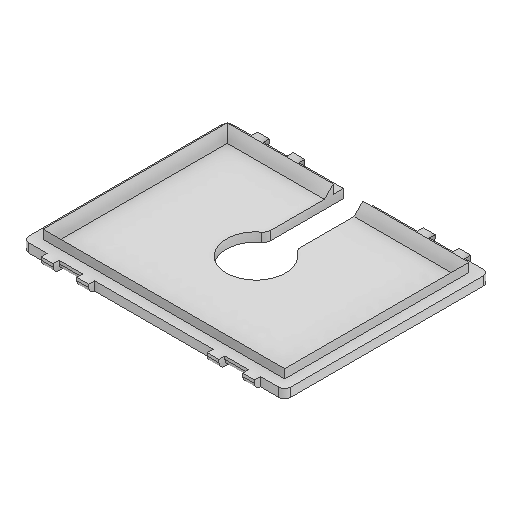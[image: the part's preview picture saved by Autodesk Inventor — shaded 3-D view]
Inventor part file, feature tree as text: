
AUTODESK INVENTOR PART (.ipt)
format: ipt  version: 2025.1 (Build 291241020, 241B)  size: 243,200 bytes
history: native  units: in
note: dims shown in document units (in); Inventor stores cm internally (conversion verified against a paired STEP export)
features: extrude x4, sketch x4, fillet x2, chamfer x1, plane x1, mirror x1
ambient origin geometry x8: Origin, YZ Plane, XZ Plane, XY Plane, X Axis, Y Axis, Z Axis, Center Point
bodies: Solid1 (feature_tree)
feature tree (13):
  extrude  "Extrusion1"  Depth=4.42in
  extrude  "Extrusion2"  Depth=0.17in
  chamfer  "Chamfer1"  Distance=0.17in
  extrude  "Extrusion3"  Depth=0.15in
  fillet  "Fillet1"  Radius=0.15in
  extrude  "Extrusion4"  Depth=0.15in TaperAngle=45.0deg
  plane  "Work Plane1"
  mirror  "Mirror1"
  fillet  "Fillet2"  Radius=1.0in
  sketch  "Sketch1"  dims[d0=3.45in d1=4.42in]
  sketch  "Sketch2"  dims[d2=0.15in d3=0.0in d4=0.17in]
  sketch  "Sketch3"  dims[d5=0.17in]
  sketch  "Sketch4"  dims[d6=0.17in d7=0.17in d8=0.15in d9=0.15in d10=0.0in d11=0.15in d12=0.125in d13=45.0deg d14=1.0in d15=2.475in d16=0.0in d17=0.5in d18=0.25in d19=0.125in d20=0.1in d21=0.2in d22=0.2in d23=0.2in d24=0.2in d25=0.4in d26=0.4in d27=2.0in d28=1.0in d29=0.1in d30=0.0in d31=0.1in]
